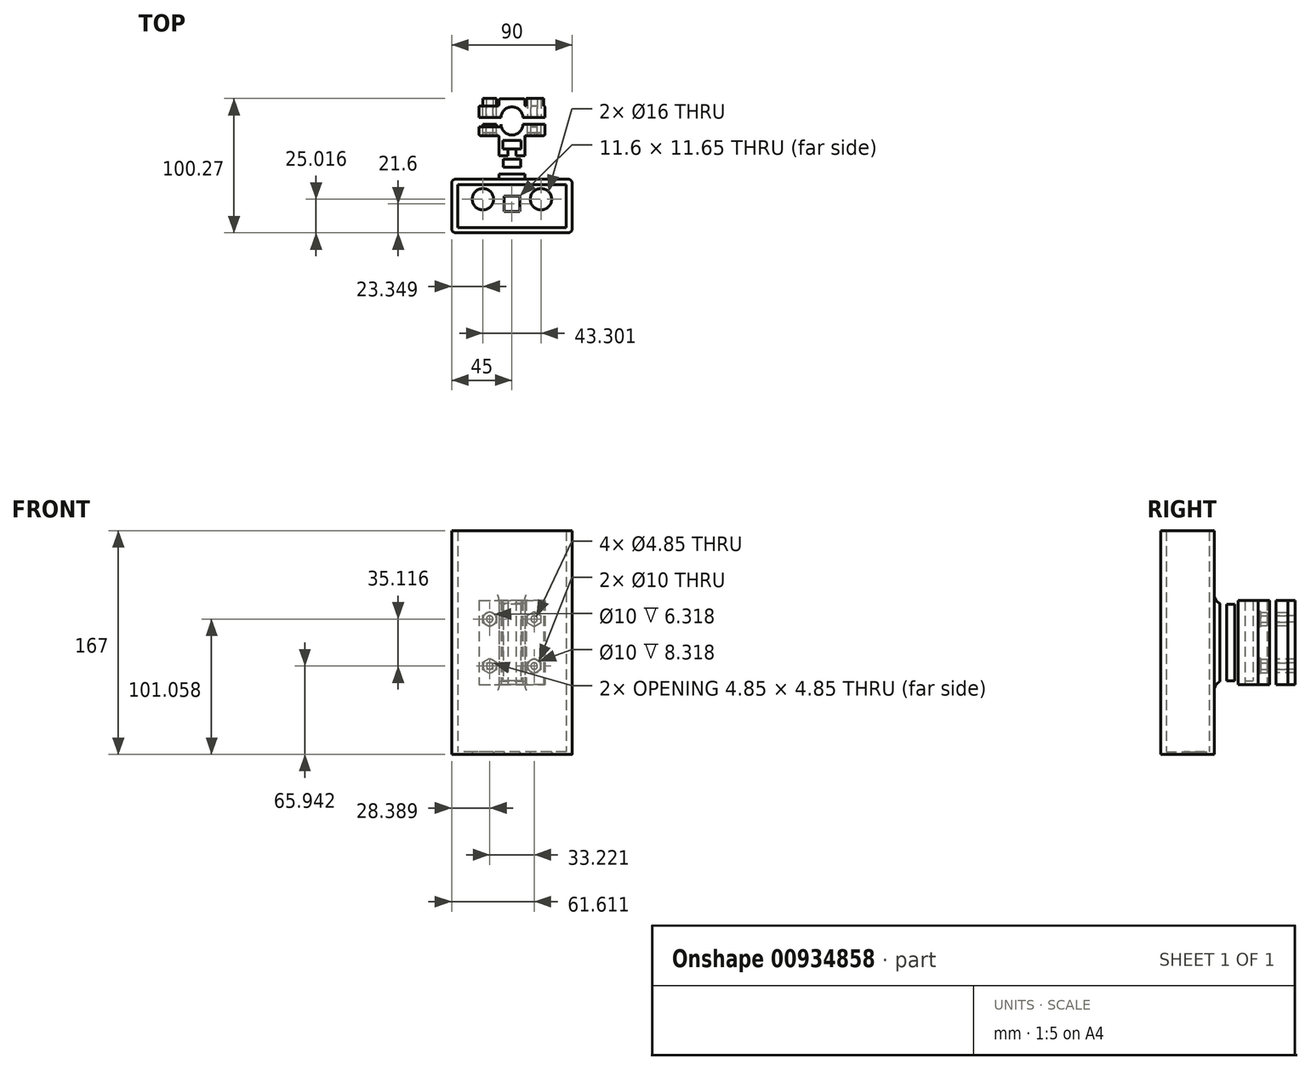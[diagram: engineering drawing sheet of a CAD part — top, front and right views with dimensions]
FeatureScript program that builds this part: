
annotation { "Feature Type Name" : "Feature", "Feature Type Description" : "" }
export const myFeature = defineFeature(function(context is Context, id is Id, definition is map)
    precondition{}
    {
        {
            var Q0;
            Q0=qCreatedBy(makeId("Top.planeOp"),FACE);
            var sketch = newSketch(context, id + "F0", { "sketchPlane" : qUnion([Q0])});
            skLineSegment(sketch, "E0.top", {"start": v(24.57, 60.93) * mm, "end": v(-24.57, 60.93) * mm});
            skLineSegment(sketch, "E1.MirrorCS", {"start": v(19.26, 60.93) * mm, "end": v(-19.26, 60.93) * mm});
            skLineSegment(sketch, "E2", {"start": v(-24.57, 56.08) * mm, "end": v(24.57, 56.08) * mm});
            skLineSegment(sketch, "E3.top", {"start": v(-23.57, 47.58) * mm, "end": v(-10.57, 47.58) * mm});
            skLineSegment(sketch, "E3.right", {"start": v(-9.57, 32.58) * mm, "end": v(-9.57, 46.58) * mm});
            skLineSegment(sketch, "E4", {"start": v(0, 15) * mm, "end": v(0, 18.42) * mm});
            skLineSegment(sketch, "E5.MirrorCS", {"start": v(9.57, 32.58) * mm, "end": v(9.57, 46.58) * mm});
            skLineSegment(sketch, "E6.MirrorCS", {"start": v(23.57, 47.58) * mm, "end": v(10.57, 47.58) * mm});
            skLineSegment(sketch, "E7", {"start": v(-24.57, 56.08) * mm, "end": v(-24.57, 48.58) * mm});
            skLineSegment(sketch, "E8", {"start": v(24.57, 56.08) * mm, "end": v(24.57, 48.58) * mm});
            skPoint(sketch, "E9.visualSharp", {"position": v(-24.57, 47.58) * mm});
            skArc(sketch, "E9.filletArc", {"start": v(-24.57, 48.58) * mm, "mid": v(-24.27, 47.88) * mm, "end": v(-23.57, 47.58) * mm});
            skPoint(sketch, "E10.visualSharp", {"position": v(24.57, 47.58) * mm});
            skArc(sketch, "E10.filletArc", {"start": v(23.57, 47.58) * mm, "mid": v(24.27, 47.88) * mm, "end": v(24.57, 48.58) * mm});
            skPoint(sketch, "E11.visualSharp", {"position": v(9.57, 47.58) * mm});
            skArc(sketch, "E11.filletArc", {"start": v(10.57, 47.58) * mm, "mid": v(9.86, 47.3) * mm, "end": v(9.57, 46.58) * mm});
            skPoint(sketch, "E12.visualSharp", {"position": v(-9.57, 47.58) * mm});
            skArc(sketch, "E12.filletArc", {"start": v(-9.57, 46.58) * mm, "mid": v(-9.86, 47.3) * mm, "end": v(-10.57, 47.58) * mm});
            skArc(sketch, "E13.filletArc", {"start": v(9.57, 16) * mm, "mid": v(9.86, 15.3) * mm, "end": v(10.57, 15) * mm});
            skArc(sketch, "E14.filletArc", {"start": v(-10.57, 15) * mm, "mid": v(-9.86, 15.3) * mm, "end": v(-9.57, 16) * mm});
            skLineSegment(sketch, "E15.bottom", {"start": v(-42.5, 75.02) * mm, "end": v(42.5, 75.02) * mm});
            skLineSegment(sketch, "E15.top", {"start": v(-42.5, 86.22) * mm, "end": v(42.5, 86.22) * mm});
            skLineSegment(sketch, "E15.left", {"start": v(-42.5, 75.02) * mm, "end": v(-42.5, 86.22) * mm});
            skLineSegment(sketch, "E15.right", {"start": v(42.5, 75.02) * mm, "end": v(42.5, 86.22) * mm});
            skLineSegment(sketch, "E16", {"start": v(-42, 15) * mm, "end": v(42, 15) * mm});
            skLineSegment(sketch, "E17", {"start": v(45, 12) * mm, "end": v(45, -22) * mm});
            skLineSegment(sketch, "E18.MirrorCS", {"start": v(-45, 12) * mm, "end": v(-45, -22) * mm});
            skLineSegment(sketch, "E19", {"start": v(48.1, -5) * mm, "end": v(55.75, -5) * mm});
            skPoint(sketch, "E19.startSnap0", {"position": v(45, -5) * mm});
            skLineSegment(sketch, "E20.MirrorCS", {"start": v(-42, -25) * mm, "end": v(42, -25) * mm});
            skPoint(sketch, "E21.visualSharp", {"position": v(-45, 15) * mm});
            skArc(sketch, "E21.filletArc", {"start": v(-42, 15) * mm, "mid": v(-44.12, 14.12) * mm, "end": v(-45, 12) * mm});
            skPoint(sketch, "E22.visualSharp", {"position": v(-45, -25) * mm});
            skArc(sketch, "E22.filletArc", {"start": v(-45, -22) * mm, "mid": v(-44.12, -24.12) * mm, "end": v(-42, -25) * mm});
            skPoint(sketch, "E23.visualSharp", {"position": v(45, -25) * mm});
            skArc(sketch, "E23.filletArc", {"start": v(42, -25) * mm, "mid": v(44.12, -24.12) * mm, "end": v(45, -22) * mm});
            skPoint(sketch, "E24.visualSharp", {"position": v(45, 15) * mm});
            skArc(sketch, "E24.filletArc", {"start": v(45, 12) * mm, "mid": v(44.12, 14.12) * mm, "end": v(42, 15) * mm});
            skPoint(sketch, "E25", {"position": v(0, -5) * mm});
            skPoint(sketch, "E25.positionSnap0", {"position": v(0, -25) * mm});
            skLineSegment(sketch, "E26.bottom", {"start": v(40.5, -21) * mm, "end": v(-40.5, -21) * mm});
            skLineSegment(sketch, "E26.top", {"start": v(40.5, 11) * mm, "end": v(-40.5, 11) * mm});
            skLineSegment(sketch, "E26.left", {"start": v(40.5, -21) * mm, "end": v(40.5, 11) * mm});
            skLineSegment(sketch, "E26.right", {"start": v(-40.5, -21) * mm, "end": v(-40.5, 11) * mm});
            skLineSegment(sketch, "E27", {"start": v(0, 1.85) * mm, "end": v(0, 11) * mm});
            skLineSegment(sketch, "E28", {"start": v(0, -8.65) * mm, "end": v(0, -19.85) * mm});
            skLineSegment(sketch, "E29.bottom", {"start": v(-5.07, 1.67) * mm, "end": v(5.07, 1.67) * mm});
            skLineSegment(sketch, "E29.top", {"start": v(-5.07, -8.47) * mm, "end": v(5.07, -8.47) * mm});
            skLineSegment(sketch, "E29.left", {"start": v(-5.07, 1.67) * mm, "end": v(-5.07, -8.47) * mm});
            skLineSegment(sketch, "E29.right", {"start": v(5.07, 1.67) * mm, "end": v(5.07, -8.47) * mm});
            skLineSegment(sketch, "E30", {"start": v(-13.65, -0.9) * mm, "end": v(-5.07, -0.9) * mm});
            skCircle(sketch, "E31", {"center": v(-21.65, 0.02) * mm, "radius": 8 * mm});
            skLineSegment(sketch, "E32", {"start": v(-21.65, 10.97) * mm, "end": v(-21.65, 8.02) * mm});
            skCircle(sketch, "E33.MirrorC", {"center": v(21.65, 0.02) * mm, "radius": 8 * mm});
            skLineSegment(sketch, "E34.MirrorCS", {"start": v(21.65, 10.97) * mm, "end": v(21.65, 8.02) * mm});
            skLineSegment(sketch, "E35", {"start": v(0, 69.01) * mm, "end": v(7.28, 69.01) * mm});
            skArc(sketch, "E36", {"start": v(8.12, 60.93) * mm, "mid": v(0, 69.01) * mm, "end": v(-8.12, 60.93) * mm});
            skLineSegment(sketch, "E37", {"start": v(0, 48) * mm, "end": v(7.28, 48) * mm});
            skArc(sketch, "E38", {"start": v(-8.12, 56.08) * mm, "mid": v(0, 48) * mm, "end": v(8.12, 56.08) * mm});
            skPoint(sketch, "E39.startSnap0", {"position": v(5.07, -3.4) * mm});
            skLineSegment(sketch, "E40.bottom", {"start": v(5.8, -9.23) * mm, "end": v(-5.8, -9.23) * mm});
            skLineSegment(sketch, "E40.top", {"start": v(5.8, 2.42) * mm, "end": v(-5.8, 2.42) * mm});
            skLineSegment(sketch, "E40.left", {"start": v(5.8, -9.23) * mm, "end": v(5.8, 2.42) * mm});
            skLineSegment(sketch, "E40.right", {"start": v(-5.8, -9.23) * mm, "end": v(-5.8, 2.42) * mm});
            skPoint(sketch, "E40.middle", {"position": v(0, -3.4) * mm});
            skLineSegment(sketch, "E41", {"start": v(24.57, 60.93) * mm, "end": v(24.57, 68.43) * mm});
            skLineSegment(sketch, "E42", {"start": v(-24.57, 60.93) * mm, "end": v(-24.57, 68.43) * mm});
            skLineSegment(sketch, "E43", {"start": v(43.87, 75.02) * mm, "end": v(51.8, 75.02) * mm});
            skLineSegment(sketch, "E44", {"start": v(-24.57, 68.43) * mm, "end": v(-24.57, 68.77) * mm});
            skLineSegment(sketch, "E45", {"start": v(-8.57, 75.02) * mm, "end": v(8.57, 75.02) * mm});
            skLineSegment(sketch, "E46", {"start": v(24.57, 68.77) * mm, "end": v(24.57, 68.43) * mm});
            skLineSegment(sketch, "E47.top", {"start": v(23.57, 69.77) * mm, "end": v(10.57, 69.77) * mm});
            skLineSegment(sketch, "E47.right", {"start": v(9.57, 74.02) * mm, "end": v(9.57, 70.77) * mm});
            skLineSegment(sketch, "E48.MirrorCS", {"start": v(-9.57, 74.02) * mm, "end": v(-9.57, 70.77) * mm});
            skLineSegment(sketch, "E49.MirrorCS", {"start": v(-23.57, 69.77) * mm, "end": v(-10.57, 69.77) * mm});
            skArc(sketch, "E50.filletArc", {"start": v(-8.57, 75.02) * mm, "mid": v(-9.27, 74.73) * mm, "end": v(-9.57, 74.02) * mm});
            skArc(sketch, "E51.filletArc", {"start": v(9.57, 74.02) * mm, "mid": v(9.27, 74.73) * mm, "end": v(8.57, 75.02) * mm});
            skArc(sketch, "E52.filletArc", {"start": v(24.57, 68.77) * mm, "mid": v(24.27, 69.47) * mm, "end": v(23.57, 69.77) * mm});
            skArc(sketch, "E53.filletArc", {"start": v(-23.57, 69.77) * mm, "mid": v(-24.27, 69.47) * mm, "end": v(-24.57, 68.77) * mm});
            skPoint(sketch, "E54.visualSharp", {"position": v(-9.57, 69.77) * mm});
            skArc(sketch, "E54.filletArc", {"start": v(-10.57, 69.77) * mm, "mid": v(-9.86, 70.06) * mm, "end": v(-9.57, 70.77) * mm});
            skPoint(sketch, "E55.visualSharp", {"position": v(9.57, 69.77) * mm});
            skArc(sketch, "E55.filletArc", {"start": v(9.57, 70.77) * mm, "mid": v(9.86, 70.06) * mm, "end": v(10.57, 69.77) * mm});
            skLineSegment(sketch, "E56", {"start": v(9.57, 18.83) * mm, "end": v(9.57, 16) * mm});
            skLineSegment(sketch, "E57", {"start": v(-9.57, 18.83) * mm, "end": v(-9.57, 16) * mm});
            skLineSegment(sketch, "E58", {"start": v(-9.57, 18.83) * mm, "end": v(9.57, 18.83) * mm});
            skLineSegment(sketch, "E59", {"start": v(-9.57, 32.58) * mm, "end": v(9.57, 32.58) * mm});
            skLineSegment(sketch, "E60.bottom", {"start": v(3.13, 32.58) * mm, "end": v(-3.13, 32.58) * mm});
            skLineSegment(sketch, "E60.top", {"start": v(3.13, 37.75) * mm, "end": v(-3.13, 37.75) * mm});
            skLineSegment(sketch, "E60.left", {"start": v(3.13, 32.58) * mm, "end": v(3.13, 37.75) * mm});
            skLineSegment(sketch, "E60.right", {"start": v(-3.13, 32.58) * mm, "end": v(-3.13, 37.75) * mm});
            skPoint(sketch, "E60.middle", {"position": v(0, 35.17) * mm});
            skLineSegment(sketch, "E61.bottom", {"start": v(6.72, 37.75) * mm, "end": v(-6.72, 37.75) * mm});
            skLineSegment(sketch, "E61.top", {"start": v(6.72, 43.84) * mm, "end": v(-6.72, 43.84) * mm});
            skLineSegment(sketch, "E61.left", {"start": v(6.72, 37.75) * mm, "end": v(6.72, 43.84) * mm});
            skLineSegment(sketch, "E61.right", {"start": v(-6.72, 37.75) * mm, "end": v(-6.72, 43.84) * mm});
            skPoint(sketch, "E61.middle", {"position": v(0, 40.8) * mm});
            skPoint(sketch, "E61.cornerSnap0", {"position": v(0, 37.75) * mm});
            skLineSegment(sketch, "E62", {"start": v(78.17, 113.73) * mm, "end": v(97.3, 113.73) * mm});
            skLineSegment(sketch, "E63.bottom", {"start": v(90.87, 113.73) * mm, "end": v(84.6, 113.73) * mm});
            skLineSegment(sketch, "E63.top", {"start": v(90.87, 118.9) * mm, "end": v(84.6, 118.9) * mm});
            skLineSegment(sketch, "E63.left", {"start": v(90.87, 113.73) * mm, "end": v(90.87, 118.9) * mm});
            skLineSegment(sketch, "E63.right", {"start": v(84.6, 113.73) * mm, "end": v(84.6, 118.9) * mm});
            skPoint(sketch, "E63.middle", {"position": v(87.74, 116.3) * mm});
            skLineSegment(sketch, "E64.bottom", {"start": v(94.46, 118.9) * mm, "end": v(81.01, 118.9) * mm});
            skLineSegment(sketch, "E64.top", {"start": v(94.46, 124.99) * mm, "end": v(81.01, 124.99) * mm});
            skLineSegment(sketch, "E64.left", {"start": v(94.46, 118.9) * mm, "end": v(94.46, 124.99) * mm});
            skLineSegment(sketch, "E64.right", {"start": v(81.01, 118.9) * mm, "end": v(81.01, 124.99) * mm});
            skPoint(sketch, "E64.middle", {"position": v(87.74, 121.94) * mm});
            skPoint(sketch, "E64.cornerSnap0", {"position": v(87.74, 118.9) * mm});
            skLineSegment(sketch, "E65.bottom", {"start": v(106.45, 86.2) * mm, "end": v(100.35, 86.2) * mm});
            skLineSegment(sketch, "E65.top", {"start": v(106.45, 91.4) * mm, "end": v(100.35, 91.4) * mm});
            skLineSegment(sketch, "E65.left", {"start": v(106.45, 86.2) * mm, "end": v(106.45, 91.4) * mm});
            skLineSegment(sketch, "E65.right", {"start": v(100.35, 86.2) * mm, "end": v(100.35, 91.4) * mm});
            skLineSegment(sketch, "E66.bottom", {"start": v(136.55, 95.24) * mm, "end": v(123.25, 95.24) * mm});
            skLineSegment(sketch, "E66.top", {"start": v(136.55, 101.24) * mm, "end": v(123.25, 101.24) * mm});
            skLineSegment(sketch, "E66.left", {"start": v(136.55, 95.24) * mm, "end": v(136.55, 101.24) * mm});
            skLineSegment(sketch, "E66.right", {"start": v(123.25, 95.24) * mm, "end": v(123.25, 101.24) * mm});
            skPoint(sketch, "E66.middle", {"position": v(129.9, 98.24) * mm});
            skLineSegment(sketch, "E67.bottom", {"start": v(6.65, 24.03) * mm, "end": v(-6.65, 24.03) * mm});
            skLineSegment(sketch, "E67.top", {"start": v(6.65, 30.03) * mm, "end": v(-6.65, 30.03) * mm});
            skLineSegment(sketch, "E67.left", {"start": v(6.65, 24.03) * mm, "end": v(6.65, 30.03) * mm});
            skLineSegment(sketch, "E67.right", {"start": v(-6.65, 24.03) * mm, "end": v(-6.65, 30.03) * mm});
            skPoint(sketch, "E67.middle", {"position": v(0, 27.03) * mm});
            skLineSegment(sketch, "E68.bottom", {"start": v(3.05, 18.83) * mm, "end": v(-3.05, 18.83) * mm});
            skLineSegment(sketch, "E68.top", {"start": v(3.05, 24.03) * mm, "end": v(-3.05, 24.03) * mm});
            skLineSegment(sketch, "E68.left", {"start": v(3.05, 18.83) * mm, "end": v(3.05, 24.03) * mm});
            skLineSegment(sketch, "E68.right", {"start": v(-3.05, 18.83) * mm, "end": v(-3.05, 24.03) * mm});
            skSolve(sketch);
        }
        {
            var Q0;
            Q0=makeQuery(id+"F0.imprint","IMPRINT",FACE,{"disambiguationData":[TD([[makeQuery(id+"F0.imprint","IMPRINT",EDGE,{"derivedFrom":sQuery(id+"F0.wireOp",EDGE,"4c624b3d-2872-479b-ac49-ad5c4bab1f2a1.MirrorCS")}),1.0]])]});
            var Q1;
            Q1=makeQuery(id+"F0.imprint","IMPRINT",FACE,{"disambiguationData":[TD([[makeQuery(id+"F0.imprint","IMPRINT",EDGE,{"derivedFrom":sQuery(id+"F0.wireOp",EDGE,"E3.top")}),1.0]])]});
            var Q2;
            Q2=makeQuery(id+"F0.imprint","IMPRINT",FACE,{"disambiguationData":[TD([[makeQuery(id+"F0.imprint","IMPRINT",EDGE,{"derivedFrom":sQuery(id+"F0.wireOp",EDGE,"YsuCSRE0-92Lo-7DDL-iV8Z-JpWwbyTIX6ej.bottom")}),-1.0]])]});
            var Q3;
            Q3=makeQuery(id+"F0.imprint","IMPRINT",FACE,{"disambiguationData":[TD([[makeQuery(id+"F0.imprint","IMPRINT",EDGE,{"derivedFrom":sQuery(id+"F0.wireOp",EDGE,"fbfb4974-d756-4670-9be3-3f5738f1f50f2.MirrorCS")}),-1.0]])]});
            var Q4;
            Q4=makeQuery(id+"F0.imprint","IMPRINT",FACE,{"disambiguationData":[TD([[makeQuery(id+"F0.imprint","IMPRINT",EDGE,{"derivedFrom":sQuery(id+"F0.wireOp",EDGE,"iMygD4c1-Gc1z-810Y-f9fB-2qDc09aOb2EL")}),-1.0]])]});
            var Q5;
            Q5=makeQuery(id+"F0.imprint","IMPRINT",FACE,{"disambiguationData":[TD([[makeQuery(id+"F0.imprint","IMPRINT",EDGE,{"derivedFrom":sQuery(id+"F0.wireOp",EDGE,"E17")}),-1.0]])]});
            var Q6;
            {var subQ5=sQuery(id+"F0.wireOp",EDGE,"E41");Q6=makeQuery(id+"F0.imprint","IMPRINT",FACE,{"disambiguationData":[TD([[makeQuery(id+"F0.imprint","IMPRINT",EDGE,{"derivedFrom":subQ5}),1.0]])]});}
            extrude(context, id + "F1", {"entities" : qUnion([Q0, Q1, Q2, Q3, Q4, Q5, Q6]), "depth" : 167 * mm, "offsetDistance" : 25 * mm});
        }
        {
            var Q0;
            Q0=makeQuery(id+"F0.imprint","IMPRINT",FACE,{"disambiguationData":[TD([[makeQuery(id+"F0.imprint","IMPRINT",EDGE,{"derivedFrom":sQuery(id+"F0.wireOp",EDGE,"E61.top")}),1.0]])]});
            var Q1;
            Q1=makeQuery(id+"F0.imprint","IMPRINT",FACE,{"disambiguationData":[TD([[makeQuery(id+"F0.imprint","IMPRINT",EDGE,{"derivedFrom":sQuery(id+"F0.wireOp",EDGE,"E60.bottom")}),-1.0]])]});
            extrude(context, id + "F2", {"entities" : qUnion([Q0, Q1]), "operationType" : NewBodyOperationType.ADD, "depth" : 55 * mm, "offsetDistance" : 25 * mm});
        }
        {
            var Q0;
            {var subQ2=sQuery(id+"F0.wireOp",EDGE,"E13.filletArc");Q0=makeQuery(id+"F0.imprint","IMPRINT",FACE,{"disambiguationData":[TD([[makeQuery(id+"F0.imprint","IMPRINT",EDGE,{"derivedFrom":subQ2}),-1.0]])]});}
            var Q1;
            Q1=makeQuery(id+"F0.imprint","IMPRINT",FACE,{"disambiguationData":[TD([[makeQuery(id+"F0.imprint","IMPRINT",EDGE,{"derivedFrom":sQuery(id+"F0.wireOp",EDGE,"E68.bottom")}),-1.0]])]});
            var Q2;
            Q2=makeQuery(id+"F0.imprint","IMPRINT",FACE,{"disambiguationData":[TD([[makeQuery(id+"F0.imprint","IMPRINT",EDGE,{"derivedFrom":sQuery(id+"F0.wireOp",EDGE,"E67.top")}),1.0]])]});
            extrude(context, id + "F3", {"entities" : qUnion([Q0, Q1, Q2]), "operationType" : NewBodyOperationType.ADD, "depth" : 150 * mm, "offsetDistance" : 25 * mm});
        }
        {
            var Q0;
            Q0=makeQuery(id+"F1.opExtrude","SWEPT_FACE",FACE,{"disambiguationData":[OSD([sQuery(id+"F0.wireOp",EDGE,"E7")])]});
            var sketch = newSketch(context, id + "F4", { "sketchPlane" : qUnion([Q0])});
            skLineSegment(sketch, "E69", {"start": v(22, 83.5) * mm, "end": v(7, 83.5) * mm});
            skLineSegment(sketch, "E70.left", {"start": v(-97.8, 0) * mm, "end": v(-97.8, 48) * mm});
            skLineSegment(sketch, "E71", {"start": v(-129.52, 55) * mm, "end": v(-129.52, 0) * mm});
            skLineSegment(sketch, "E72.bottom", {"start": v(-140.7, 0) * mm, "end": v(-129.52, 0) * mm});
            skLineSegment(sketch, "E72.top", {"start": v(-140.7, 55) * mm, "end": v(-129.52, 55) * mm});
            skLineSegment(sketch, "E72.left", {"start": v(-140.7, 0) * mm, "end": v(-140.7, 55) * mm});
            skLineSegment(sketch, "E72.right", {"start": v(-129.52, 0) * mm, "end": v(-129.52, 55) * mm});
            skLineSegment(sketch, "E73.bottom", {"start": v(-140.7, 167) * mm, "end": v(-129.52, 167) * mm});
            skLineSegment(sketch, "E73.top", {"start": v(-140.7, 112) * mm, "end": v(-129.52, 112) * mm});
            skLineSegment(sketch, "E73.left", {"start": v(-140.7, 167) * mm, "end": v(-140.7, 112) * mm});
            skLineSegment(sketch, "E73.right", {"start": v(-129.52, 167) * mm, "end": v(-129.52, 112) * mm});
            skLineSegment(sketch, "E74.bottom", {"start": v(-129.52, 0) * mm, "end": v(-97.8, 0) * mm});
            skLineSegment(sketch, "E74.top", {"start": v(-129.52, 55) * mm, "end": v(-104.8, 55) * mm});
            skPoint(sketch, "E75.visualSharp", {"position": v(-97.8, 55) * mm});
            skArc(sketch, "E75.filletArc", {"start": v(-97.8, 48) * mm, "mid": v(-99.85, 52.95) * mm, "end": v(-104.8, 55) * mm});
            skLineSegment(sketch, "E76.bottom", {"start": v(-129.52, 167) * mm, "end": v(-97.8, 167) * mm});
            skLineSegment(sketch, "E76.top", {"start": v(-129.52, 112) * mm, "end": v(-104.8, 112) * mm});
            skLineSegment(sketch, "E76.right", {"start": v(-97.8, 167) * mm, "end": v(-97.8, 119) * mm});
            skPoint(sketch, "E77.visualSharp", {"position": v(-97.8, 112) * mm});
            skArc(sketch, "E77.filletArc", {"start": v(-104.8, 112) * mm, "mid": v(-99.85, 114.05) * mm, "end": v(-97.8, 119) * mm});
            skPoint(sketch, "E78", {"position": v(-15, 167) * mm});
            skPoint(sketch, "E79", {"position": v(-32.58, 167) * mm});
            skLineSegment(sketch, "E80.bottom", {"start": v(-15, 167) * mm, "end": v(-32.58, 167) * mm});
            skLineSegment(sketch, "E80.top", {"start": v(-22, 112) * mm, "end": v(-32.58, 112) * mm});
            skLineSegment(sketch, "E80.left", {"start": v(-15, 167) * mm, "end": v(-15, 119) * mm});
            skLineSegment(sketch, "E80.right", {"start": v(-32.58, 167) * mm, "end": v(-32.58, 112) * mm});
            skPoint(sketch, "E81.visualSharp", {"position": v(-15, 112) * mm});
            skArc(sketch, "E81.filletArc", {"start": v(-22, 112) * mm, "mid": v(-17.05, 114.05) * mm, "end": v(-15, 119) * mm});
            skLineSegment(sketch, "E82.bottom", {"start": v(-15, 0) * mm, "end": v(-32.58, 0) * mm});
            skLineSegment(sketch, "E82.top", {"start": v(-22, 55) * mm, "end": v(-32.58, 55) * mm});
            skLineSegment(sketch, "E82.left", {"start": v(-15, 0) * mm, "end": v(-15, 48) * mm});
            skLineSegment(sketch, "E82.right", {"start": v(-32.58, 0) * mm, "end": v(-32.58, 55) * mm});
            skPoint(sketch, "E83.visualSharp", {"position": v(-15, 55) * mm});
            skArc(sketch, "E83.filletArc", {"start": v(-15, 48) * mm, "mid": v(-17.05, 52.95) * mm, "end": v(-22, 55) * mm});
            skSolve(sketch);
        }
        {
            var Q0;
            Q0=makeQuery(id+"F1.opExtrude","SWEPT_FACE",FACE,{"disambiguationData":[OSD([sQuery(id+"F0.wireOp",EDGE,"E42"),sQuery(id+"F0.wireOp",EDGE,"E44")])]});
            var sketch = newSketch(context, id + "F5", { "sketchPlane" : qUnion([Q0])});
            skLineSegment(sketch, "E84", {"start": v(56.64, 2.48) * mm, "end": v(41.64, 2.48) * mm});
            skLineSegment(sketch, "E85.bottom", {"start": v(-32.58, 52.14) * mm, "end": v(-46.58, 52.14) * mm});
            skLineSegment(sketch, "E85.top", {"start": v(-32.58, 114.86) * mm, "end": v(-46.58, 114.86) * mm});
            skLineSegment(sketch, "E85.left", {"start": v(-32.58, 52.14) * mm, "end": v(-32.58, 114.86) * mm});
            skLineSegment(sketch, "E85.right", {"start": v(-46.58, 52.14) * mm, "end": v(-46.58, 114.86) * mm});
            skPoint(sketch, "E85.middle", {"position": v(-39.58, 83.5) * mm});
            skPoint(sketch, "E85.middle.positionSnap0", {"position": v(-32.58, 83.5) * mm});
            skPoint(sketch, "E85.middle.positionSnap1", {"position": v(-39.58, 167) * mm});
            skPoint(sketch, "E85.centerSnap0", {"position": v(-32.58, 83.5) * mm});
            skPoint(sketch, "E85.centerSnap1", {"position": v(-39.58, 167) * mm});
            skLineSegment(sketch, "E86.bottom", {"start": v(-32.58, 167) * mm, "end": v(-46.58, 167) * mm});
            skLineSegment(sketch, "E86.left", {"start": v(-32.58, 167) * mm, "end": v(-32.58, 114.86) * mm});
            skLineSegment(sketch, "E86.right", {"start": v(-46.58, 167) * mm, "end": v(-46.58, 114.86) * mm});
            skLineSegment(sketch, "E87.bottom", {"start": v(-32.58, 0) * mm, "end": v(-46.58, 0) * mm});
            skLineSegment(sketch, "E87.left", {"start": v(-32.58, 0) * mm, "end": v(-32.58, 52.14) * mm});
            skLineSegment(sketch, "E87.right", {"start": v(-46.58, 0) * mm, "end": v(-46.58, 52.14) * mm});
            skLineSegment(sketch, "E88.bottom", {"start": v(-46.58, 114.86) * mm, "end": v(-76.2, 114.86) * mm});
            skLineSegment(sketch, "E88.top", {"start": v(-46.58, 167) * mm, "end": v(-76.2, 167) * mm});
            skLineSegment(sketch, "E88.left", {"start": v(-46.58, 114.86) * mm, "end": v(-46.58, 167) * mm});
            skLineSegment(sketch, "E88.right", {"start": v(-76.2, 114.86) * mm, "end": v(-76.2, 167) * mm});
            skLineSegment(sketch, "E89.bottom", {"start": v(-46.58, 0) * mm, "end": v(-76.2, 0) * mm});
            skLineSegment(sketch, "E89.top", {"start": v(-46.58, 52.14) * mm, "end": v(-76.2, 52.14) * mm});
            skLineSegment(sketch, "E89.right", {"start": v(-76.2, 0) * mm, "end": v(-76.2, 52.14) * mm});
            skSolve(sketch);
        }
        {
            var Q0;
            {var subQ3=sQuery(id+"F4.wireOp",EDGE,"E82.right");Q0=makeQuery(id+"F4.imprint","IMPRINT",FACE,{"disambiguationData":[TD([[makeQuery(id+"F4.imprint","IMPRINT",EDGE,{"derivedFrom":subQ3}),-1.0]])]});}
            var Q1;
            Q1=makeQuery(id+"F4.imprint","IMPRINT",FACE,{"disambiguationData":[TD([[makeQuery(id+"F4.imprint","IMPRINT",EDGE,{"derivedFrom":sQuery(id+"F4.wireOp",EDGE,"E80.bottom")}),1.0]])]});
            extrude(context, id + "F6", {"entities" : qUnion([Q0, Q1]), "operationType" : NewBodyOperationType.REMOVE, "oppositeDirection" : true, "depth" : 85 * mm, "offsetDistance" : 25 * mm});
        }
        {
            var Q0;
            Q0=makeQuery(id+"F5.imprint","IMPRINT",FACE,{"disambiguationData":[TD([[makeQuery(id+"F5.imprint","IMPRINT",EDGE,{"derivedFrom":sQuery(id+"F5.wireOp",EDGE,"E86.bottom")}),1.0]])]});
            var Q1;
            Q1=makeQuery(id+"F5.imprint","IMPRINT",FACE,{"disambiguationData":[TD([[makeQuery(id+"F5.imprint","IMPRINT",EDGE,{"derivedFrom":sQuery(id+"F5.wireOp",EDGE,"E87.bottom")}),-1.0]])]});
            var Q2;
            Q2=makeQuery(id+"F5.imprint","IMPRINT",FACE,{"disambiguationData":[TD([[makeQuery(id+"F5.imprint","IMPRINT",EDGE,{"derivedFrom":sQuery(id+"F5.wireOp",EDGE,"E88.bottom")}),-1.0]])]});
            var Q3;
            Q3=makeQuery(id+"F5.imprint","IMPRINT",FACE,{"disambiguationData":[TD([[makeQuery(id+"F5.imprint","IMPRINT",EDGE,{"derivedFrom":sQuery(id+"F5.wireOp",EDGE,"E89.bottom")}),-1.0]])]});
            extrude(context, id + "F7", {"entities" : qUnion([Q0, Q1, Q2, Q3]), "operationType" : NewBodyOperationType.REMOVE, "oppositeDirection" : true, "depth" : 85 * mm, "offsetDistance" : 25 * mm});
        }
        {
            var Q0;
            Q0=makeQuery(id+"F1.opExtrude","SWEPT_FACE",FACE,{"disambiguationData":[OSD([sQuery(id+"F0.wireOp",EDGE,"E47.top")])]});
            var sketch = newSketch(context, id + "F8", { "sketchPlane" : qUnion([Q0])});
            skLineSegment(sketch, "E90", {"start": v(-9.66, 83.5) * mm, "end": v(-15.89, 83.5) * mm});
            skLineSegment(sketch, "E91", {"start": v(-16.61, 106.5) * mm, "end": v(-16.61, 55) * mm});
            skCircle(sketch, "E92", {"center": v(-16.61, 101.06) * mm, "radius": 5 * mm});
            skCircle(sketch, "E93", {"center": v(-16.61, 101.06) * mm, "radius": 2.43 * mm});
            skCircle(sketch, "E94.MirrorC", {"center": v(-16.61, 65.94) * mm, "radius": 5 * mm});
            skCircle(sketch, "E95.MirrorC", {"center": v(-16.61, 65.94) * mm, "radius": 2.43 * mm});
            skCircle(sketch, "E96.MirrorC", {"center": v(16.61, 101.06) * mm, "radius": 5 * mm});
            skCircle(sketch, "E97.MirrorC", {"center": v(16.61, 101.06) * mm, "radius": 2.43 * mm});
            skCircle(sketch, "E98.MirrorC", {"center": v(16.61, 65.94) * mm, "radius": 5 * mm});
            skCircle(sketch, "E99.MirrorC", {"center": v(16.61, 65.94) * mm, "radius": 2.43 * mm});
            skLineSegment(sketch, "E100", {"start": v(0, 112.05) * mm, "end": v(0, 102.58) * mm});
            skSolve(sketch);
        }
        {
            var Q0;
            Q0=makeQuery(id+"F8.imprint","IMPRINT",FACE,{"disambiguationData":[TD([[makeQuery(id+"F8.imprint","IMPRINT",EDGE,{"derivedFrom":sQuery(id+"F8.wireOp",EDGE,"E92")}),1.0]])]});
            var Q1;
            Q1=makeQuery(id+"F8.imprint","IMPRINT",FACE,{"disambiguationData":[TD([[makeQuery(id+"F8.imprint","IMPRINT",EDGE,{"derivedFrom":sQuery(id+"F8.wireOp",EDGE,"b0e11951-a132-40b3-9681-b4b9e884a0070.MirrorC")}),-1.0]])]});
            var Q2;
            Q2=makeQuery(id+"F8.imprint","IMPRINT",FACE,{"disambiguationData":[TD([[makeQuery(id+"F8.imprint","IMPRINT",EDGE,{"derivedFrom":sQuery(id+"F8.wireOp",EDGE,"0375aff9-4b0e-4836-b45d-683225d9ef240.MirrorC")}),1.0]])]});
            var Q3;
            Q3=makeQuery(id+"F8.imprint","IMPRINT",FACE,{"disambiguationData":[TD([[makeQuery(id+"F8.imprint","IMPRINT",EDGE,{"derivedFrom":sQuery(id+"F8.wireOp",EDGE,"1b341e29-3375-4108-860d-d1da36d85cfd0.MirrorC")}),-1.0]])]});
            var Q4;
            Q4=makeQuery(id+"F8.imprint","IMPRINT",FACE,{"disambiguationData":[TD([[makeQuery(id+"F8.imprint","IMPRINT",EDGE,{"derivedFrom":sQuery(id+"F8.wireOp",EDGE,"E94.MirrorC")}),-1.0]])]});
            var Q5;
            Q5=makeQuery(id+"F8.imprint","IMPRINT",FACE,{"disambiguationData":[TD([[makeQuery(id+"F8.imprint","IMPRINT",EDGE,{"derivedFrom":sQuery(id+"F8.wireOp",EDGE,"E96.MirrorC")}),-1.0]])]});
            var Q6;
            Q6=makeQuery(id+"F8.imprint","IMPRINT",FACE,{"disambiguationData":[TD([[makeQuery(id+"F8.imprint","IMPRINT",EDGE,{"derivedFrom":sQuery(id+"F8.wireOp",EDGE,"E98.MirrorC")}),1.0]])]});
            extrude(context, id + "F9", {"entities" : qUnion([Q0, Q1, Q2, Q3, Q4, Q5, Q6]), "operationType" : NewBodyOperationType.ADD, "depth" : 5.5 * mm, "offsetDistance" : 25 * mm});
        }
        {
            var Q0;
            Q0=makeQuery(id+"F8.imprint","IMPRINT",FACE,{"disambiguationData":[TD([[makeQuery(id+"F8.imprint","IMPRINT",EDGE,{"derivedFrom":sQuery(id+"F8.wireOp",EDGE,"E93")}),1.0]])]});
            var Q1;
            Q1=makeQuery(id+"F8.imprint","IMPRINT",FACE,{"disambiguationData":[TD([[makeQuery(id+"F8.imprint","IMPRINT",EDGE,{"derivedFrom":sQuery(id+"F8.wireOp",EDGE,"E97.MirrorC")}),-1.0]])]});
            var Q2;
            Q2=makeQuery(id+"F8.imprint","IMPRINT",FACE,{"disambiguationData":[TD([[makeQuery(id+"F8.imprint","IMPRINT",EDGE,{"derivedFrom":sQuery(id+"F8.wireOp",EDGE,"E99.MirrorC")}),1.0]])]});
            var Q3;
            Q3=makeQuery(id+"F8.imprint","IMPRINT",FACE,{"disambiguationData":[TD([[makeQuery(id+"F8.imprint","IMPRINT",EDGE,{"derivedFrom":sQuery(id+"F8.wireOp",EDGE,"E95.MirrorC")}),-1.0]])]});
            extrude(context, id + "F10", {"entities" : qUnion([Q0, Q1, Q2, Q3]), "operationType" : NewBodyOperationType.REMOVE, "oppositeDirection" : true, "depth" : 22 * mm, "offsetDistance" : 25 * mm});
        }
        {
            var Q0;
            Q0=makeQuery(id+"F1.opExtrude","SWEPT_FACE",FACE,{"disambiguationData":[OSD([sQuery(id+"F0.wireOp",EDGE,"E6.MirrorCS")])]});
            var sketch = newSketch(context, id + "F11", { "sketchPlane" : qUnion([Q0])});
            skCircle(sketch, "E101.cCircle", {"center": v(-16.61, 101.06) * mm, "radius": 4.98 * mm, "construction": true});
            skLineSegment(sketch, "E101.0", {"start": v(-11.63, 103.93) * mm, "end": v(-11.63, 98.18) * mm});
            skLineSegment(sketch, "E101.1", {"start": v(-11.63, 98.18) * mm, "end": v(-16.61, 95.3) * mm});
            skLineSegment(sketch, "E101.2", {"start": v(-16.61, 95.3) * mm, "end": v(-21.6, 98.18) * mm});
            skLineSegment(sketch, "E101.3", {"start": v(-21.6, 98.18) * mm, "end": v(-21.6, 103.93) * mm});
            skLineSegment(sketch, "E101.4", {"start": v(-21.6, 103.93) * mm, "end": v(-16.61, 106.8) * mm});
            skLineSegment(sketch, "E101.5", {"start": v(-16.61, 106.8) * mm, "end": v(-11.63, 103.93) * mm});
            skPoint(sketch, "E101.0.midPoint", {"position": v(-11.63, 101.06) * mm});
            skCircle(sketch, "E102.cCircle", {"center": v(-16.61, 65.94) * mm, "radius": 4.98 * mm, "construction": true});
            skLineSegment(sketch, "E102.0", {"start": v(-11.63, 68.82) * mm, "end": v(-11.63, 63.07) * mm});
            skLineSegment(sketch, "E102.1", {"start": v(-11.63, 63.07) * mm, "end": v(-16.61, 60.2) * mm});
            skLineSegment(sketch, "E102.2", {"start": v(-16.61, 60.2) * mm, "end": v(-21.6, 63.07) * mm});
            skLineSegment(sketch, "E102.3", {"start": v(-21.6, 63.07) * mm, "end": v(-21.6, 68.82) * mm});
            skLineSegment(sketch, "E102.4", {"start": v(-21.6, 68.82) * mm, "end": v(-16.61, 71.7) * mm});
            skLineSegment(sketch, "E102.5", {"start": v(-16.61, 71.7) * mm, "end": v(-11.63, 68.82) * mm});
            skPoint(sketch, "E102.0.midPoint", {"position": v(-11.63, 65.94) * mm});
            skCircle(sketch, "E103.cCircle", {"center": v(16.61, 101.06) * mm, "radius": 4.98 * mm, "construction": true});
            skLineSegment(sketch, "E103.0", {"start": v(11.63, 98.18) * mm, "end": v(11.63, 103.93) * mm});
            skLineSegment(sketch, "E103.1", {"start": v(11.63, 103.93) * mm, "end": v(16.61, 106.8) * mm});
            skLineSegment(sketch, "E103.2", {"start": v(16.61, 106.8) * mm, "end": v(21.6, 103.93) * mm});
            skLineSegment(sketch, "E103.3", {"start": v(21.6, 103.93) * mm, "end": v(21.6, 98.18) * mm});
            skLineSegment(sketch, "E103.4", {"start": v(21.6, 98.18) * mm, "end": v(16.61, 95.3) * mm});
            skLineSegment(sketch, "E103.5", {"start": v(16.61, 95.3) * mm, "end": v(11.63, 98.18) * mm});
            skPoint(sketch, "E103.0.midPoint", {"position": v(11.63, 101.06) * mm});
            skCircle(sketch, "E104.cCircle", {"center": v(16.61, 65.94) * mm, "radius": 4.98 * mm, "construction": true});
            skLineSegment(sketch, "E104.0", {"start": v(11.63, 63.07) * mm, "end": v(11.63, 68.82) * mm});
            skLineSegment(sketch, "E104.1", {"start": v(11.63, 68.82) * mm, "end": v(16.61, 71.7) * mm});
            skLineSegment(sketch, "E104.2", {"start": v(16.61, 71.7) * mm, "end": v(21.6, 68.82) * mm});
            skLineSegment(sketch, "E104.3", {"start": v(21.6, 68.82) * mm, "end": v(21.6, 63.07) * mm});
            skLineSegment(sketch, "E104.4", {"start": v(21.6, 63.07) * mm, "end": v(16.61, 60.2) * mm});
            skLineSegment(sketch, "E104.5", {"start": v(16.61, 60.2) * mm, "end": v(11.63, 63.07) * mm});
            skPoint(sketch, "E104.0.midPoint", {"position": v(11.63, 65.94) * mm});
            skSolve(sketch);
        }
        {
            var Q0;
            Q0=makeQuery(id+"F11.imprint","IMPRINT",FACE,{"disambiguationData":[TD([[makeQuery(id+"F11.imprint","IMPRINT",EDGE,{"derivedFrom":sQuery(id+"F11.wireOp",EDGE,"E101.0")}),-1.0]])]});
            var Q1;
            Q1=makeQuery(id+"F11.imprint","IMPRINT",FACE,{"disambiguationData":[TD([[makeQuery(id+"F11.imprint","IMPRINT",EDGE,{"derivedFrom":sQuery(id+"F11.wireOp",EDGE,"E102.0")}),-1.0]])]});
            var Q2;
            Q2=makeQuery(id+"F11.imprint","IMPRINT",FACE,{"disambiguationData":[TD([[makeQuery(id+"F11.imprint","IMPRINT",EDGE,{"derivedFrom":sQuery(id+"F11.wireOp",EDGE,"E103.0")}),-1.0]])]});
            var Q3;
            Q3=makeQuery(id+"F11.imprint","IMPRINT",FACE,{"disambiguationData":[TD([[makeQuery(id+"F11.imprint","IMPRINT",EDGE,{"derivedFrom":sQuery(id+"F11.wireOp",EDGE,"E104.0")}),-1.0]])]});
            extrude(context, id + "F12", {"entities" : qUnion([Q0, Q1, Q2, Q3]), "operationType" : NewBodyOperationType.REMOVE, "oppositeDirection" : true, "depth" : 2 * mm, "offsetDistance" : 25 * mm});
        }
        {
            var Q0;
            Q0=makeQuery(id+"F0.imprint","IMPRINT",FACE,{"disambiguationData":[TD([[makeQuery(id+"F0.imprint","IMPRINT",EDGE,{"derivedFrom":sQuery(id+"F0.wireOp",EDGE,"OqUKywtR-sI8F-MxQy-PJir-ycoHASkRKoPq.bottom")}),-1.0]])]});
            var Q1;
            Q1=makeQuery(id+"F0.imprint","IMPRINT",FACE,{"disambiguationData":[TD([[makeQuery(id+"F0.imprint","IMPRINT",EDGE,{"derivedFrom":sQuery(id+"F0.wireOp",EDGE,"E26.bottom")}),-1.0]])]});
            extrude(context, id + "F13", {"entities" : qUnion([Q0, Q1]), "operationType" : NewBodyOperationType.ADD, "depth" : 2 * mm, "offsetDistance" : 25 * mm});
        }
        {
            var Q0;
            {var subQ0=sQuery(id+"F0.wireOp",EDGE,"E2");Q0=makeQuery(id+"F1.opExtrude","SWEPT_FACE",FACE,{"disambiguationData":[OSD([subQ0]),TDD([makeQuery(id+"F0.imprint","IMPRINT",EDGE,{"disambiguationData":[TD([[makeQuery(id+"F0.imprint","INTERSECT",VERTEX,{"derivedFrom":[subQ0,sQuery(id+"F0.wireOp",EDGE,"E7")]}),-1.0]])],"derivedFrom":subQ0})])]});}
            var sketch = newSketch(context, id + "F14", { "sketchPlane" : qUnion([Q0])});
            skCircle(sketch, "E105", {"center": v(16.61, 101.06) * mm, "radius": 4.98 * mm});
            skLineSegment(sketch, "E106", {"start": v(24.57, 83.5) * mm, "end": v(15.81, 83.5) * mm});
            skCircle(sketch, "E107.MirrorC", {"center": v(16.61, 65.94) * mm, "radius": 4.98 * mm});
            skLineSegment(sketch, "E108", {"start": v(0, 112) * mm, "end": v(0, 22.58) * mm});
            skCircle(sketch, "E109.MirrorC", {"center": v(-16.61, 101.06) * mm, "radius": 4.98 * mm});
            skCircle(sketch, "E110.MirrorC", {"center": v(-16.61, 65.94) * mm, "radius": 4.98 * mm});
            skSolve(sketch);
        }
        {
            var Q0;
            Q0=makeQuery(id+"F14.imprint","IMPRINT",FACE,{"disambiguationData":[TD([[makeQuery(id+"F14.imprint","IMPRINT",EDGE,{"derivedFrom":sQuery(id+"F14.wireOp",EDGE,"E105")}),1.0]])]});
            var Q1;
            Q1=makeQuery(id+"F14.imprint","IMPRINT",FACE,{"disambiguationData":[TD([[makeQuery(id+"F14.imprint","IMPRINT",EDGE,{"derivedFrom":sQuery(id+"F14.wireOp",EDGE,"E107.MirrorC")}),-1.0]])]});
            var Q2;
            Q2=makeQuery(id+"F14.imprint","IMPRINT",FACE,{"disambiguationData":[TD([[makeQuery(id+"F14.imprint","IMPRINT",EDGE,{"derivedFrom":sQuery(id+"F14.wireOp",EDGE,"E110.MirrorC")}),1.0]])]});
            var Q3;
            Q3=makeQuery(id+"F14.imprint","IMPRINT",FACE,{"disambiguationData":[TD([[makeQuery(id+"F14.imprint","IMPRINT",EDGE,{"derivedFrom":sQuery(id+"F14.wireOp",EDGE,"E109.MirrorC")}),-1.0]])]});
            extrude(context, id + "F15", {"entities" : qUnion([Q0, Q1, Q2, Q3]), "operationType" : NewBodyOperationType.REMOVE, "oppositeDirection" : true, "depth" : 2 * mm, "offsetDistance" : 25 * mm});
        }
    });
